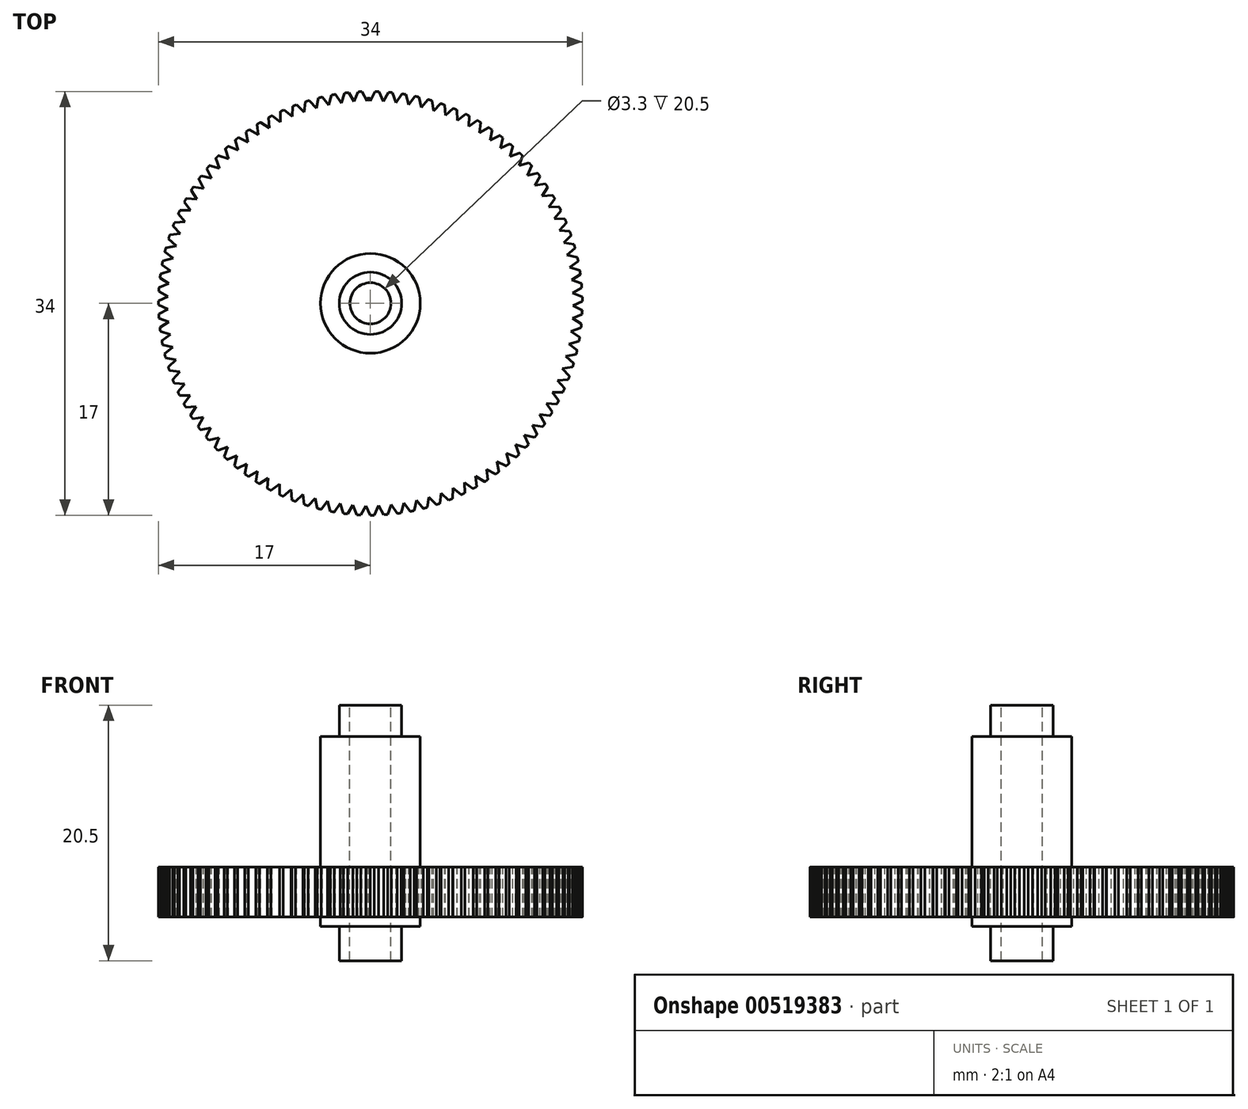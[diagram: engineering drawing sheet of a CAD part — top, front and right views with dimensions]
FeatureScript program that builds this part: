
annotation { "Feature Type Name" : "Feature", "Feature Type Description" : "" }
export const myFeature = defineFeature(function(context is Context, id is Id, definition is map)
    precondition{}
    {
        {
            var Q0;
            Q0=qCreatedBy(makeId("Top.planeOp"),FACE);
            var sketch = newSketch(context, id + "F0", { "sketchPlane" : qUnion([Q0])});
            skCircle(sketch, "E0", {"center": v(0, 0) * mm, "radius": 17 * mm});
            skSolve(sketch);
        }
        {
            var Q0;
            Q0 = qSketchRegion(id + "F0", true);
            extrude(context, id + "F1", {"entities" : qUnion([Q0]), "depth" : 4 * mm, "offsetDistance" : 25 * mm});
        }
        {
            var Q0;
            Q0=makeQuery(id+"F1.opExtrude","CAP_FACE",FACE,{"disambiguationData":[OSD([sQuery(id+"F0.wireOp",EDGE,"E0")])],"isStart":false});
            var sketch = newSketch(context, id + "F2", { "sketchPlane" : qUnion([Q0])});
            skLineSegment(sketch, "E1", {"start": v(-0.37, 17) * mm, "end": v(0, 16.25) * mm});
            skLineSegment(sketch, "E2", {"start": v(0, 16.25) * mm, "end": v(0.38, 17) * mm});
            skLineSegment(sketch, "E3", {"start": v(-0.37, 17) * mm, "end": v(0, 17.76) * mm});
            skLineSegment(sketch, "E4", {"start": v(0, 17.76) * mm, "end": v(0.38, 17) * mm});
            skLineSegment(sketch, "E5.1.0", {"start": v(1.03, 16.21) * mm, "end": v(1.45, 16.94) * mm});
            skLineSegment(sketch, "E5.1.1", {"start": v(0.7, 16.99) * mm, "end": v(1.03, 16.21) * mm});
            skLineSegment(sketch, "E5.1.2", {"start": v(1.12, 17.73) * mm, "end": v(1.45, 16.94) * mm});
            skLineSegment(sketch, "E5.1.3", {"start": v(0.7, 16.99) * mm, "end": v(1.12, 17.73) * mm});
            skLineSegment(sketch, "E5.2.0", {"start": v(2.05, 16.12) * mm, "end": v(2.52, 16.81) * mm});
            skLineSegment(sketch, "E5.2.1", {"start": v(1.77, 16.9) * mm, "end": v(2.05, 16.12) * mm});
            skLineSegment(sketch, "E5.2.2", {"start": v(2.24, 17.62) * mm, "end": v(2.52, 16.81) * mm});
            skLineSegment(sketch, "E5.2.3", {"start": v(1.77, 16.9) * mm, "end": v(2.24, 17.62) * mm});
            skPoint(sketch, "E5.center", {"position": v(0, 0) * mm});
            skLineSegment(sketch, "E5.anchor1", {"start": v(0, 0) * mm, "end": v(0, 16.25) * mm, "construction": true});
            skLineSegment(sketch, "E5.anchor2", {"start": v(0, 0) * mm, "end": v(-0.28, 16.24) * mm, "construction": true});
            skLineSegment(sketch, "E6.1.3.0", {"start": v(3.07, 15.95) * mm, "end": v(3.58, 16.62) * mm});
            skLineSegment(sketch, "E6.3.3.0", {"start": v(2.84, 16.76) * mm, "end": v(3.07, 15.95) * mm});
            skLineSegment(sketch, "E6.6.3.0", {"start": v(3.35, 17.44) * mm, "end": v(3.58, 16.62) * mm});
            skLineSegment(sketch, "E6.9.3.0", {"start": v(2.84, 16.76) * mm, "end": v(3.35, 17.44) * mm});
            skLineSegment(sketch, "E6.1.4.0", {"start": v(4.07, 15.73) * mm, "end": v(4.62, 16.36) * mm});
            skLineSegment(sketch, "E6.3.4.0", {"start": v(3.9, 16.55) * mm, "end": v(4.07, 15.73) * mm});
            skLineSegment(sketch, "E6.6.4.0", {"start": v(4.45, 17.2) * mm, "end": v(4.62, 16.36) * mm});
            skLineSegment(sketch, "E6.9.4.0", {"start": v(3.9, 16.55) * mm, "end": v(4.45, 17.2) * mm});
            skLineSegment(sketch, "E6.1.5.0", {"start": v(5.06, 15.44) * mm, "end": v(5.65, 16.04) * mm});
            skLineSegment(sketch, "E6.3.5.0", {"start": v(4.93, 16.27) * mm, "end": v(5.06, 15.44) * mm});
            skLineSegment(sketch, "E6.6.5.0", {"start": v(5.53, 16.88) * mm, "end": v(5.65, 16.04) * mm});
            skLineSegment(sketch, "E6.9.5.0", {"start": v(4.93, 16.27) * mm, "end": v(5.53, 16.88) * mm});
            skLineSegment(sketch, "E6.1.6.0", {"start": v(6.02, 15.09) * mm, "end": v(6.65, 15.65) * mm});
            skLineSegment(sketch, "E6.3.6.0", {"start": v(5.95, 15.92) * mm, "end": v(6.02, 15.09) * mm});
            skLineSegment(sketch, "E6.6.6.0", {"start": v(6.58, 16.5) * mm, "end": v(6.65, 15.65) * mm});
            skLineSegment(sketch, "E6.9.6.0", {"start": v(5.95, 15.92) * mm, "end": v(6.58, 16.5) * mm});
            skLineSegment(sketch, "E6.1.7.0", {"start": v(6.96, 14.68) * mm, "end": v(7.62, 15.2) * mm});
            skLineSegment(sketch, "E6.3.7.0", {"start": v(6.95, 15.52) * mm, "end": v(6.96, 14.68) * mm});
            skLineSegment(sketch, "E6.6.7.0", {"start": v(7.61, 16.05) * mm, "end": v(7.62, 15.2) * mm});
            skLineSegment(sketch, "E6.9.7.0", {"start": v(6.95, 15.52) * mm, "end": v(7.61, 16.05) * mm});
            skLineSegment(sketch, "E6.1.8.0", {"start": v(7.88, 14.2) * mm, "end": v(8.57, 14.68) * mm});
            skLineSegment(sketch, "E6.3.8.0", {"start": v(7.91, 15.05) * mm, "end": v(7.88, 14.2) * mm});
            skLineSegment(sketch, "E6.6.8.0", {"start": v(8.61, 15.53) * mm, "end": v(8.57, 14.68) * mm});
            skLineSegment(sketch, "E6.9.8.0", {"start": v(7.91, 15.05) * mm, "end": v(8.61, 15.53) * mm});
            skLineSegment(sketch, "E6.1.9.0", {"start": v(8.76, 13.68) * mm, "end": v(9.48, 14.11) * mm});
            skLineSegment(sketch, "E6.3.9.0", {"start": v(8.85, 14.51) * mm, "end": v(8.76, 13.68) * mm});
            skLineSegment(sketch, "E6.6.9.0", {"start": v(9.58, 14.96) * mm, "end": v(9.48, 14.11) * mm});
            skLineSegment(sketch, "E6.9.9.0", {"start": v(8.85, 14.51) * mm, "end": v(9.58, 14.96) * mm});
            skLineSegment(sketch, "E6.1.10.0", {"start": v(9.6, 13.1) * mm, "end": v(10.36, 13.48) * mm});
            skLineSegment(sketch, "E6.3.10.0", {"start": v(9.75, 13.93) * mm, "end": v(9.6, 13.1) * mm});
            skLineSegment(sketch, "E6.6.10.0", {"start": v(10.5, 14.32) * mm, "end": v(10.36, 13.48) * mm});
            skLineSegment(sketch, "E6.9.10.0", {"start": v(9.75, 13.93) * mm, "end": v(10.5, 14.32) * mm});
            skLineSegment(sketch, "E6.1.11.0", {"start": v(10.42, 12.47) * mm, "end": v(11.19, 12.8) * mm});
            skLineSegment(sketch, "E6.3.11.0", {"start": v(10.61, 13.28) * mm, "end": v(10.42, 12.47) * mm});
            skLineSegment(sketch, "E6.6.11.0", {"start": v(11.4, 13.63) * mm, "end": v(11.19, 12.8) * mm});
            skLineSegment(sketch, "E6.9.11.0", {"start": v(10.61, 13.28) * mm, "end": v(11.4, 13.63) * mm});
            skLineSegment(sketch, "E6.1.12.0", {"start": v(11.19, 11.78) * mm, "end": v(11.97, 12.07) * mm});
            skLineSegment(sketch, "E6.3.12.0", {"start": v(11.43, 12.58) * mm, "end": v(11.19, 11.78) * mm});
            skLineSegment(sketch, "E6.6.12.0", {"start": v(12.23, 12.88) * mm, "end": v(11.97, 12.07) * mm});
            skLineSegment(sketch, "E6.9.12.0", {"start": v(11.43, 12.58) * mm, "end": v(12.23, 12.88) * mm});
            skLineSegment(sketch, "E6.1.13.0", {"start": v(11.9, 11.05) * mm, "end": v(12.71, 11.29) * mm});
            skLineSegment(sketch, "E6.3.13.0", {"start": v(12.2, 11.84) * mm, "end": v(11.9, 11.05) * mm});
            skLineSegment(sketch, "E6.6.13.0", {"start": v(13.02, 12.08) * mm, "end": v(12.71, 11.29) * mm});
            skLineSegment(sketch, "E6.9.13.0", {"start": v(12.2, 11.84) * mm, "end": v(13.02, 12.08) * mm});
            skLineSegment(sketch, "E6.1.14.0", {"start": v(12.58, 10.27) * mm, "end": v(13.4, 10.46) * mm});
            skLineSegment(sketch, "E6.3.14.0", {"start": v(12.93, 11.04) * mm, "end": v(12.58, 10.27) * mm});
            skLineSegment(sketch, "E6.6.14.0", {"start": v(13.76, 11.23) * mm, "end": v(13.4, 10.46) * mm});
            skLineSegment(sketch, "E6.9.14.0", {"start": v(12.93, 11.04) * mm, "end": v(13.76, 11.23) * mm});
            skLineSegment(sketch, "E6.1.15.0", {"start": v(13.2, 9.46) * mm, "end": v(14.04, 9.6) * mm});
            skLineSegment(sketch, "E6.3.15.0", {"start": v(13.6, 10.2) * mm, "end": v(13.2, 9.46) * mm});
            skLineSegment(sketch, "E6.6.15.0", {"start": v(14.44, 10.34) * mm, "end": v(14.04, 9.6) * mm});
            skLineSegment(sketch, "E6.9.15.0", {"start": v(13.6, 10.2) * mm, "end": v(14.44, 10.34) * mm});
            skLineSegment(sketch, "E6.1.16.0", {"start": v(13.78, 8.6) * mm, "end": v(14.62, 8.68) * mm});
            skLineSegment(sketch, "E6.3.16.0", {"start": v(14.22, 9.32) * mm, "end": v(13.78, 8.6) * mm});
            skLineSegment(sketch, "E6.6.16.0", {"start": v(15.07, 9.4) * mm, "end": v(14.62, 8.68) * mm});
            skLineSegment(sketch, "E6.9.16.0", {"start": v(14.22, 9.32) * mm, "end": v(15.07, 9.4) * mm});
            skLineSegment(sketch, "E6.1.17.0", {"start": v(14.3, 7.72) * mm, "end": v(15.14, 7.74) * mm});
            skLineSegment(sketch, "E6.3.17.0", {"start": v(14.78, 8.4) * mm, "end": v(14.3, 7.72) * mm});
            skLineSegment(sketch, "E6.6.17.0", {"start": v(15.63, 8.44) * mm, "end": v(15.14, 7.74) * mm});
            skLineSegment(sketch, "E6.9.17.0", {"start": v(14.78, 8.4) * mm, "end": v(15.63, 8.44) * mm});
            skLineSegment(sketch, "E6.1.18.0", {"start": v(14.76, 6.8) * mm, "end": v(15.6, 6.77) * mm});
            skLineSegment(sketch, "E6.3.18.0", {"start": v(15.28, 7.45) * mm, "end": v(14.76, 6.8) * mm});
            skLineSegment(sketch, "E6.6.18.0", {"start": v(16.13, 7.43) * mm, "end": v(15.6, 6.77) * mm});
            skLineSegment(sketch, "E6.9.18.0", {"start": v(15.28, 7.45) * mm, "end": v(16.13, 7.43) * mm});
            skLineSegment(sketch, "E6.1.19.0", {"start": v(15.16, 5.85) * mm, "end": v(16, 5.77) * mm});
            skLineSegment(sketch, "E6.3.19.0", {"start": v(15.72, 6.47) * mm, "end": v(15.16, 5.85) * mm});
            skLineSegment(sketch, "E6.6.19.0", {"start": v(16.57, 6.4) * mm, "end": v(16, 5.77) * mm});
            skLineSegment(sketch, "E6.9.19.0", {"start": v(15.72, 6.47) * mm, "end": v(16.57, 6.4) * mm});
            skLineSegment(sketch, "E6.1.20.0", {"start": v(15.5, 4.88) * mm, "end": v(16.32, 4.75) * mm});
            skLineSegment(sketch, "E6.3.20.0", {"start": v(16.1, 5.46) * mm, "end": v(15.5, 4.88) * mm});
            skLineSegment(sketch, "E6.6.20.0", {"start": v(16.94, 5.33) * mm, "end": v(16.32, 4.75) * mm});
            skLineSegment(sketch, "E6.9.20.0", {"start": v(16.1, 5.46) * mm, "end": v(16.94, 5.33) * mm});
            skLineSegment(sketch, "E6.1.21.0", {"start": v(15.77, 3.89) * mm, "end": v(16.6, 3.7) * mm});
            skLineSegment(sketch, "E6.3.21.0", {"start": v(16.41, 4.43) * mm, "end": v(15.77, 3.89) * mm});
            skLineSegment(sketch, "E6.6.21.0", {"start": v(17.25, 4.25) * mm, "end": v(16.6, 3.7) * mm});
            skLineSegment(sketch, "E6.9.21.0", {"start": v(16.41, 4.43) * mm, "end": v(17.25, 4.25) * mm});
            skLineSegment(sketch, "E6.1.22.0", {"start": v(15.99, 2.88) * mm, "end": v(16.8, 2.65) * mm});
            skLineSegment(sketch, "E6.3.22.0", {"start": v(16.66, 3.39) * mm, "end": v(15.99, 2.88) * mm});
            skLineSegment(sketch, "E6.6.22.0", {"start": v(17.48, 3.15) * mm, "end": v(16.8, 2.65) * mm});
            skLineSegment(sketch, "E6.9.22.0", {"start": v(16.66, 3.39) * mm, "end": v(17.48, 3.15) * mm});
            skLineSegment(sketch, "E6.1.23.0", {"start": v(16.14, 1.87) * mm, "end": v(16.93, 1.58) * mm});
            skLineSegment(sketch, "E6.3.23.0", {"start": v(16.84, 2.32) * mm, "end": v(16.14, 1.87) * mm});
            skLineSegment(sketch, "E6.6.23.0", {"start": v(17.64, 2.04) * mm, "end": v(16.93, 1.58) * mm});
            skLineSegment(sketch, "E6.9.23.0", {"start": v(16.84, 2.32) * mm, "end": v(17.64, 2.04) * mm});
            skLineSegment(sketch, "E6.1.24.0", {"start": v(16.22, 0.84) * mm, "end": v(17, 0.5) * mm});
            skLineSegment(sketch, "E6.3.24.0", {"start": v(16.95, 1.26) * mm, "end": v(16.22, 0.84) * mm});
            skLineSegment(sketch, "E6.6.24.0", {"start": v(17.74, 0.92) * mm, "end": v(17, 0.5) * mm});
            skLineSegment(sketch, "E6.9.24.0", {"start": v(16.95, 1.26) * mm, "end": v(17.74, 0.92) * mm});
            skLineSegment(sketch, "E6.1.25.0", {"start": v(16.24, -0.19) * mm, "end": v(17, -0.57) * mm});
            skLineSegment(sketch, "E6.3.25.0", {"start": v(17, 0.18) * mm, "end": v(16.24, -0.19) * mm});
            skLineSegment(sketch, "E6.6.25.0", {"start": v(17.76, -0.2) * mm, "end": v(17, -0.57) * mm});
            skLineSegment(sketch, "E6.9.25.0", {"start": v(17, 0.18) * mm, "end": v(17.76, -0.2) * mm});
            skLineSegment(sketch, "E6.1.26.0", {"start": v(16.2, -1.21) * mm, "end": v(16.92, -1.64) * mm});
            skLineSegment(sketch, "E6.3.26.0", {"start": v(16.98, -0.9) * mm, "end": v(16.2, -1.21) * mm});
            skLineSegment(sketch, "E6.6.26.0", {"start": v(17.71, -1.33) * mm, "end": v(16.92, -1.64) * mm});
            skLineSegment(sketch, "E6.9.26.0", {"start": v(16.98, -0.9) * mm, "end": v(17.71, -1.33) * mm});
            skLineSegment(sketch, "E6.1.27.0", {"start": v(16.1, -2.24) * mm, "end": v(16.78, -2.71) * mm});
            skLineSegment(sketch, "E6.3.27.0", {"start": v(16.89, -1.97) * mm, "end": v(16.1, -2.24) * mm});
            skLineSegment(sketch, "E6.6.27.0", {"start": v(17.6, -2.44) * mm, "end": v(16.78, -2.71) * mm});
            skLineSegment(sketch, "E6.9.27.0", {"start": v(16.89, -1.97) * mm, "end": v(17.6, -2.44) * mm});
            skLineSegment(sketch, "E6.1.28.0", {"start": v(15.92, -3.25) * mm, "end": v(16.58, -3.77) * mm});
            skLineSegment(sketch, "E6.3.28.0", {"start": v(16.73, -3.03) * mm, "end": v(15.92, -3.25) * mm});
            skLineSegment(sketch, "E6.6.28.0", {"start": v(17.4, -3.55) * mm, "end": v(16.58, -3.77) * mm});
            skLineSegment(sketch, "E6.9.28.0", {"start": v(16.73, -3.03) * mm, "end": v(17.4, -3.55) * mm});
            skLineSegment(sketch, "E6.1.29.0", {"start": v(15.68, -4.25) * mm, "end": v(16.3, -4.8) * mm});
            skLineSegment(sketch, "E6.3.29.0", {"start": v(16.5, -4.08) * mm, "end": v(15.68, -4.25) * mm});
            skLineSegment(sketch, "E6.6.29.0", {"start": v(17.14, -4.65) * mm, "end": v(16.3, -4.8) * mm});
            skLineSegment(sketch, "E6.9.29.0", {"start": v(16.5, -4.08) * mm, "end": v(17.14, -4.65) * mm});
            skLineSegment(sketch, "E6.1.30.0", {"start": v(15.38, -5.23) * mm, "end": v(15.97, -5.83) * mm});
            skLineSegment(sketch, "E6.3.30.0", {"start": v(16.21, -5.12) * mm, "end": v(15.38, -5.23) * mm});
            skLineSegment(sketch, "E6.6.30.0", {"start": v(16.82, -5.72) * mm, "end": v(15.97, -5.83) * mm});
            skLineSegment(sketch, "E6.9.30.0", {"start": v(16.21, -5.12) * mm, "end": v(16.82, -5.72) * mm});
            skLineSegment(sketch, "E6.1.31.0", {"start": v(15.02, -6.2) * mm, "end": v(15.57, -6.83) * mm});
            skLineSegment(sketch, "E6.3.31.0", {"start": v(15.85, -6.13) * mm, "end": v(15.02, -6.2) * mm});
            skLineSegment(sketch, "E6.6.31.0", {"start": v(16.42, -6.77) * mm, "end": v(15.57, -6.83) * mm});
            skLineSegment(sketch, "E6.9.31.0", {"start": v(15.85, -6.13) * mm, "end": v(16.42, -6.77) * mm});
            skLineSegment(sketch, "E6.1.32.0", {"start": v(14.6, -7.13) * mm, "end": v(15.1, -7.8) * mm});
            skLineSegment(sketch, "E6.3.32.0", {"start": v(15.44, -7.12) * mm, "end": v(14.6, -7.13) * mm});
            skLineSegment(sketch, "E6.6.32.0", {"start": v(15.96, -7.8) * mm, "end": v(15.1, -7.8) * mm});
            skLineSegment(sketch, "E6.9.32.0", {"start": v(15.44, -7.12) * mm, "end": v(15.96, -7.8) * mm});
            skLineSegment(sketch, "E6.1.33.0", {"start": v(14.12, -8.04) * mm, "end": v(14.58, -8.74) * mm});
            skLineSegment(sketch, "E6.3.33.0", {"start": v(14.95, -8.09) * mm, "end": v(14.12, -8.04) * mm});
            skLineSegment(sketch, "E6.6.33.0", {"start": v(15.43, -8.8) * mm, "end": v(14.58, -8.74) * mm});
            skLineSegment(sketch, "E6.9.33.0", {"start": v(14.95, -8.09) * mm, "end": v(15.43, -8.8) * mm});
            skLineSegment(sketch, "E6.1.34.0", {"start": v(13.58, -8.92) * mm, "end": v(14, -9.64) * mm});
            skLineSegment(sketch, "E6.3.34.0", {"start": v(14.41, -9.02) * mm, "end": v(13.58, -8.92) * mm});
            skLineSegment(sketch, "E6.6.34.0", {"start": v(14.85, -9.75) * mm, "end": v(14, -9.64) * mm});
            skLineSegment(sketch, "E6.9.34.0", {"start": v(14.41, -9.02) * mm, "end": v(14.85, -9.75) * mm});
            skLineSegment(sketch, "E6.1.35.0", {"start": v(12.99, -9.76) * mm, "end": v(13.36, -10.5) * mm});
            skLineSegment(sketch, "E6.3.35.0", {"start": v(13.81, -9.9) * mm, "end": v(12.99, -9.76) * mm});
            skLineSegment(sketch, "E6.6.35.0", {"start": v(14.2, -10.67) * mm, "end": v(13.36, -10.5) * mm});
            skLineSegment(sketch, "E6.9.35.0", {"start": v(13.81, -9.9) * mm, "end": v(14.2, -10.67) * mm});
            skLineSegment(sketch, "E6.1.36.0", {"start": v(12.35, -10.56) * mm, "end": v(12.67, -11.33) * mm});
            skLineSegment(sketch, "E6.3.36.0", {"start": v(13.16, -10.76) * mm, "end": v(12.35, -10.56) * mm});
            skLineSegment(sketch, "E6.6.36.0", {"start": v(13.5, -11.55) * mm, "end": v(12.67, -11.33) * mm});
            skLineSegment(sketch, "E6.9.36.0", {"start": v(13.16, -10.76) * mm, "end": v(13.5, -11.55) * mm});
            skLineSegment(sketch, "E6.1.37.0", {"start": v(11.65, -11.32) * mm, "end": v(11.93, -12.11) * mm});
            skLineSegment(sketch, "E6.3.37.0", {"start": v(12.45, -11.57) * mm, "end": v(11.65, -11.32) * mm});
            skLineSegment(sketch, "E6.6.37.0", {"start": v(12.74, -12.38) * mm, "end": v(11.93, -12.11) * mm});
            skLineSegment(sketch, "E6.9.37.0", {"start": v(12.45, -11.57) * mm, "end": v(12.74, -12.38) * mm});
            skLineSegment(sketch, "E6.1.38.0", {"start": v(10.91, -12.03) * mm, "end": v(11.14, -12.84) * mm});
            skLineSegment(sketch, "E6.3.38.0", {"start": v(11.7, -12.34) * mm, "end": v(10.91, -12.03) * mm});
            skLineSegment(sketch, "E6.6.38.0", {"start": v(11.93, -13.16) * mm, "end": v(11.14, -12.84) * mm});
            skLineSegment(sketch, "E6.9.38.0", {"start": v(11.7, -12.34) * mm, "end": v(11.93, -13.16) * mm});
            skLineSegment(sketch, "E6.1.39.0", {"start": v(10.13, -12.7) * mm, "end": v(10.3, -13.52) * mm});
            skLineSegment(sketch, "E6.3.39.0", {"start": v(10.9, -13.05) * mm, "end": v(10.13, -12.7) * mm});
            skLineSegment(sketch, "E6.6.39.0", {"start": v(11.08, -13.89) * mm, "end": v(10.3, -13.52) * mm});
            skLineSegment(sketch, "E6.9.39.0", {"start": v(10.9, -13.05) * mm, "end": v(11.08, -13.89) * mm});
            skLineSegment(sketch, "E6.1.40.0", {"start": v(9.3, -13.32) * mm, "end": v(9.43, -14.15) * mm});
            skLineSegment(sketch, "E6.3.40.0", {"start": v(10.04, -13.72) * mm, "end": v(9.3, -13.32) * mm});
            skLineSegment(sketch, "E6.6.40.0", {"start": v(10.18, -14.56) * mm, "end": v(9.43, -14.15) * mm});
            skLineSegment(sketch, "E6.9.40.0", {"start": v(10.04, -13.72) * mm, "end": v(10.18, -14.56) * mm});
            skLineSegment(sketch, "E6.1.41.0", {"start": v(8.45, -13.88) * mm, "end": v(8.52, -14.71) * mm});
            skLineSegment(sketch, "E6.3.41.0", {"start": v(9.16, -14.32) * mm, "end": v(8.45, -13.88) * mm});
            skLineSegment(sketch, "E6.6.41.0", {"start": v(9.23, -15.17) * mm, "end": v(8.52, -14.71) * mm});
            skLineSegment(sketch, "E6.9.41.0", {"start": v(9.16, -14.32) * mm, "end": v(9.23, -15.17) * mm});
            skLineSegment(sketch, "E6.1.42.0", {"start": v(7.55, -14.38) * mm, "end": v(7.57, -15.22) * mm});
            skLineSegment(sketch, "E6.3.42.0", {"start": v(8.23, -14.87) * mm, "end": v(7.55, -14.38) * mm});
            skLineSegment(sketch, "E6.6.42.0", {"start": v(8.26, -15.73) * mm, "end": v(7.57, -15.22) * mm});
            skLineSegment(sketch, "E6.9.42.0", {"start": v(8.23, -14.87) * mm, "end": v(8.26, -15.73) * mm});
            skLineSegment(sketch, "E6.1.43.0", {"start": v(6.63, -14.83) * mm, "end": v(6.59, -15.67) * mm});
            skLineSegment(sketch, "E6.3.43.0", {"start": v(7.27, -15.37) * mm, "end": v(6.63, -14.83) * mm});
            skLineSegment(sketch, "E6.6.43.0", {"start": v(7.24, -16.22) * mm, "end": v(6.59, -15.67) * mm});
            skLineSegment(sketch, "E6.9.43.0", {"start": v(7.27, -15.37) * mm, "end": v(7.24, -16.22) * mm});
            skLineSegment(sketch, "E6.1.44.0", {"start": v(5.67, -15.22) * mm, "end": v(5.59, -16.06) * mm});
            skLineSegment(sketch, "E6.3.44.0", {"start": v(6.29, -15.8) * mm, "end": v(5.67, -15.22) * mm});
            skLineSegment(sketch, "E6.6.44.0", {"start": v(6.2, -16.64) * mm, "end": v(5.59, -16.06) * mm});
            skLineSegment(sketch, "E6.9.44.0", {"start": v(6.29, -15.8) * mm, "end": v(6.2, -16.64) * mm});
            skLineSegment(sketch, "E6.1.45.0", {"start": v(4.7, -15.55) * mm, "end": v(4.56, -16.38) * mm});
            skLineSegment(sketch, "E6.3.45.0", {"start": v(5.28, -16.16) * mm, "end": v(4.7, -15.55) * mm});
            skLineSegment(sketch, "E6.6.45.0", {"start": v(5.14, -17) * mm, "end": v(4.56, -16.38) * mm});
            skLineSegment(sketch, "E6.9.45.0", {"start": v(5.28, -16.16) * mm, "end": v(5.14, -17) * mm});
            skLineSegment(sketch, "E6.1.46.0", {"start": v(3.7, -15.82) * mm, "end": v(3.51, -16.63) * mm});
            skLineSegment(sketch, "E6.3.46.0", {"start": v(4.24, -16.46) * mm, "end": v(3.7, -15.82) * mm});
            skLineSegment(sketch, "E6.6.46.0", {"start": v(4.05, -17.3) * mm, "end": v(3.51, -16.63) * mm});
            skLineSegment(sketch, "E6.9.46.0", {"start": v(4.24, -16.46) * mm, "end": v(4.05, -17.3) * mm});
            skLineSegment(sketch, "E6.1.47.0", {"start": v(2.7, -16.02) * mm, "end": v(2.45, -16.82) * mm});
            skLineSegment(sketch, "E6.3.47.0", {"start": v(3.2, -16.7) * mm, "end": v(2.7, -16.02) * mm});
            skLineSegment(sketch, "E6.6.47.0", {"start": v(2.95, -17.52) * mm, "end": v(2.45, -16.82) * mm});
            skLineSegment(sketch, "E6.9.47.0", {"start": v(3.2, -16.7) * mm, "end": v(2.95, -17.52) * mm});
            skLineSegment(sketch, "E6.1.48.0", {"start": v(1.68, -16.16) * mm, "end": v(1.39, -16.94) * mm});
            skLineSegment(sketch, "E6.3.48.0", {"start": v(2.13, -16.87) * mm, "end": v(1.68, -16.16) * mm});
            skLineSegment(sketch, "E6.6.48.0", {"start": v(1.84, -17.67) * mm, "end": v(1.39, -16.94) * mm});
            skLineSegment(sketch, "E6.9.48.0", {"start": v(2.13, -16.87) * mm, "end": v(1.84, -17.67) * mm});
            skLineSegment(sketch, "E6.1.49.0", {"start": v(0.66, -16.23) * mm, "end": v(0.31, -17) * mm});
            skLineSegment(sketch, "E6.3.49.0", {"start": v(1.06, -16.97) * mm, "end": v(0.66, -16.23) * mm});
            skLineSegment(sketch, "E6.6.49.0", {"start": v(0.72, -17.75) * mm, "end": v(0.31, -17) * mm});
            skLineSegment(sketch, "E6.9.49.0", {"start": v(1.06, -16.97) * mm, "end": v(0.72, -17.75) * mm});
            skLineSegment(sketch, "E6.1.50.0", {"start": v(-0.37, -16.24) * mm, "end": v(-0.76, -16.98) * mm});
            skLineSegment(sketch, "E6.3.50.0", {"start": v(-0.01, -17) * mm, "end": v(-0.37, -16.24) * mm});
            skLineSegment(sketch, "E6.6.50.0", {"start": v(-0.4, -17.76) * mm, "end": v(-0.76, -16.98) * mm});
            skLineSegment(sketch, "E6.9.50.0", {"start": v(-0.01, -17) * mm, "end": v(-0.4, -17.76) * mm});
            skLineSegment(sketch, "E6.1.51.0", {"start": v(-1.4, -16.19) * mm, "end": v(-1.84, -16.9) * mm});
            skLineSegment(sketch, "E6.3.51.0", {"start": v(-1.09, -16.97) * mm, "end": v(-1.4, -16.19) * mm});
            skLineSegment(sketch, "E6.6.51.0", {"start": v(-1.53, -17.7) * mm, "end": v(-1.84, -16.9) * mm});
            skLineSegment(sketch, "E6.9.51.0", {"start": v(-1.09, -16.97) * mm, "end": v(-1.53, -17.7) * mm});
            skLineSegment(sketch, "E6.1.52.0", {"start": v(-2.42, -16.06) * mm, "end": v(-2.9, -16.75) * mm});
            skLineSegment(sketch, "E6.3.52.0", {"start": v(-2.16, -16.86) * mm, "end": v(-2.42, -16.06) * mm});
            skLineSegment(sketch, "E6.6.52.0", {"start": v(-2.65, -17.56) * mm, "end": v(-2.9, -16.75) * mm});
            skLineSegment(sketch, "E6.9.52.0", {"start": v(-2.16, -16.86) * mm, "end": v(-2.65, -17.56) * mm});
            skLineSegment(sketch, "E6.1.53.0", {"start": v(-3.43, -15.88) * mm, "end": v(-3.96, -16.53) * mm});
            skLineSegment(sketch, "E6.3.53.0", {"start": v(-3.22, -16.7) * mm, "end": v(-3.43, -15.88) * mm});
            skLineSegment(sketch, "E6.6.53.0", {"start": v(-3.75, -17.36) * mm, "end": v(-3.96, -16.53) * mm});
            skLineSegment(sketch, "E6.9.53.0", {"start": v(-3.22, -16.7) * mm, "end": v(-3.75, -17.36) * mm});
            skLineSegment(sketch, "E6.1.54.0", {"start": v(-4.43, -15.63) * mm, "end": v(-5, -16.25) * mm});
            skLineSegment(sketch, "E6.3.54.0", {"start": v(-4.27, -16.45) * mm, "end": v(-4.43, -15.63) * mm});
            skLineSegment(sketch, "E6.6.54.0", {"start": v(-4.84, -17.09) * mm, "end": v(-5, -16.25) * mm});
            skLineSegment(sketch, "E6.9.54.0", {"start": v(-4.27, -16.45) * mm, "end": v(-4.84, -17.09) * mm});
            skLineSegment(sketch, "E6.1.55.0", {"start": v(-5.4, -15.32) * mm, "end": v(-6.01, -15.9) * mm});
            skLineSegment(sketch, "E6.3.55.0", {"start": v(-5.3, -16.15) * mm, "end": v(-5.4, -15.32) * mm});
            skLineSegment(sketch, "E6.6.55.0", {"start": v(-5.91, -16.75) * mm, "end": v(-6.01, -15.9) * mm});
            skLineSegment(sketch, "E6.9.55.0", {"start": v(-5.3, -16.15) * mm, "end": v(-5.91, -16.75) * mm});
            skLineSegment(sketch, "E6.1.56.0", {"start": v(-6.37, -14.95) * mm, "end": v(-7, -15.49) * mm});
            skLineSegment(sketch, "E6.3.56.0", {"start": v(-6.32, -15.78) * mm, "end": v(-6.37, -14.95) * mm});
            skLineSegment(sketch, "E6.6.56.0", {"start": v(-6.96, -16.34) * mm, "end": v(-7, -15.49) * mm});
            skLineSegment(sketch, "E6.9.56.0", {"start": v(-6.32, -15.78) * mm, "end": v(-6.96, -16.34) * mm});
            skLineSegment(sketch, "E6.1.57.0", {"start": v(-7.3, -14.51) * mm, "end": v(-7.97, -15.02) * mm});
            skLineSegment(sketch, "E6.3.57.0", {"start": v(-7.3, -15.35) * mm, "end": v(-7.3, -14.51) * mm});
            skLineSegment(sketch, "E6.6.57.0", {"start": v(-7.98, -15.87) * mm, "end": v(-7.97, -15.02) * mm});
            skLineSegment(sketch, "E6.9.57.0", {"start": v(-7.3, -15.35) * mm, "end": v(-7.98, -15.87) * mm});
            skLineSegment(sketch, "E6.1.58.0", {"start": v(-8.2, -14.02) * mm, "end": v(-8.9, -14.48) * mm});
            skLineSegment(sketch, "E6.3.58.0", {"start": v(-8.26, -14.86) * mm, "end": v(-8.2, -14.02) * mm});
            skLineSegment(sketch, "E6.6.58.0", {"start": v(-8.97, -15.33) * mm, "end": v(-8.9, -14.48) * mm});
            skLineSegment(sketch, "E6.9.58.0", {"start": v(-8.26, -14.86) * mm, "end": v(-8.97, -15.33) * mm});
            skLineSegment(sketch, "E6.1.59.0", {"start": v(-9.07, -13.48) * mm, "end": v(-9.8, -13.89) * mm});
            skLineSegment(sketch, "E6.3.59.0", {"start": v(-9.18, -14.3) * mm, "end": v(-9.07, -13.48) * mm});
            skLineSegment(sketch, "E6.6.59.0", {"start": v(-9.92, -14.73) * mm, "end": v(-9.8, -13.89) * mm});
            skLineSegment(sketch, "E6.9.59.0", {"start": v(-9.18, -14.3) * mm, "end": v(-9.92, -14.73) * mm});
            skLineSegment(sketch, "E6.1.60.0", {"start": v(-9.9, -12.88) * mm, "end": v(-10.66, -13.24) * mm});
            skLineSegment(sketch, "E6.3.60.0", {"start": v(-10.07, -13.7) * mm, "end": v(-9.9, -12.88) * mm});
            skLineSegment(sketch, "E6.6.60.0", {"start": v(-10.83, -14.08) * mm, "end": v(-10.66, -13.24) * mm});
            skLineSegment(sketch, "E6.9.60.0", {"start": v(-10.07, -13.7) * mm, "end": v(-10.83, -14.08) * mm});
            skLineSegment(sketch, "E6.1.61.0", {"start": v(-10.7, -12.22) * mm, "end": v(-11.48, -12.54) * mm});
            skLineSegment(sketch, "E6.3.61.0", {"start": v(-10.91, -13.03) * mm, "end": v(-10.7, -12.22) * mm});
            skLineSegment(sketch, "E6.6.61.0", {"start": v(-11.7, -13.36) * mm, "end": v(-11.48, -12.54) * mm});
            skLineSegment(sketch, "E6.9.61.0", {"start": v(-10.91, -13.03) * mm, "end": v(-11.7, -13.36) * mm});
            skLineSegment(sketch, "E6.1.62.0", {"start": v(-11.45, -11.52) * mm, "end": v(-12.25, -11.79) * mm});
            skLineSegment(sketch, "E6.3.62.0", {"start": v(-11.72, -12.32) * mm, "end": v(-11.45, -11.52) * mm});
            skLineSegment(sketch, "E6.6.62.0", {"start": v(-12.52, -12.6) * mm, "end": v(-12.25, -11.79) * mm});
            skLineSegment(sketch, "E6.9.62.0", {"start": v(-11.72, -12.32) * mm, "end": v(-12.52, -12.6) * mm});
            skLineSegment(sketch, "E6.1.63.0", {"start": v(-12.16, -10.77) * mm, "end": v(-12.97, -11) * mm});
            skLineSegment(sketch, "E6.3.63.0", {"start": v(-12.47, -11.55) * mm, "end": v(-12.16, -10.77) * mm});
            skLineSegment(sketch, "E6.6.63.0", {"start": v(-13.3, -11.78) * mm, "end": v(-12.97, -11) * mm});
            skLineSegment(sketch, "E6.9.63.0", {"start": v(-12.47, -11.55) * mm, "end": v(-13.3, -11.78) * mm});
            skLineSegment(sketch, "E6.1.64.0", {"start": v(-12.82, -9.98) * mm, "end": v(-13.64, -10.15) * mm});
            skLineSegment(sketch, "E6.3.64.0", {"start": v(-13.18, -10.74) * mm, "end": v(-12.82, -9.98) * mm});
            skLineSegment(sketch, "E6.6.64.0", {"start": v(-14.01, -10.92) * mm, "end": v(-13.64, -10.15) * mm});
            skLineSegment(sketch, "E6.9.64.0", {"start": v(-13.18, -10.74) * mm, "end": v(-14.01, -10.92) * mm});
            skLineSegment(sketch, "E6.1.65.0", {"start": v(-13.42, -9.15) * mm, "end": v(-14.25, -9.27) * mm});
            skLineSegment(sketch, "E6.3.65.0", {"start": v(-13.83, -9.89) * mm, "end": v(-13.42, -9.15) * mm});
            skLineSegment(sketch, "E6.6.65.0", {"start": v(-14.67, -10) * mm, "end": v(-14.25, -9.27) * mm});
            skLineSegment(sketch, "E6.9.65.0", {"start": v(-13.83, -9.89) * mm, "end": v(-14.67, -10) * mm});
            skLineSegment(sketch, "E6.1.66.0", {"start": v(-13.97, -8.29) * mm, "end": v(-14.81, -8.35) * mm});
            skLineSegment(sketch, "E6.3.66.0", {"start": v(-14.43, -9) * mm, "end": v(-13.97, -8.29) * mm});
            skLineSegment(sketch, "E6.6.66.0", {"start": v(-15.28, -9.06) * mm, "end": v(-14.81, -8.35) * mm});
            skLineSegment(sketch, "E6.9.66.0", {"start": v(-14.43, -9) * mm, "end": v(-15.28, -9.06) * mm});
            skLineSegment(sketch, "E6.1.67.0", {"start": v(-14.47, -7.39) * mm, "end": v(-15.3, -7.4) * mm});
            skLineSegment(sketch, "E6.3.67.0", {"start": v(-14.97, -8.06) * mm, "end": v(-14.47, -7.39) * mm});
            skLineSegment(sketch, "E6.6.67.0", {"start": v(-15.82, -8.08) * mm, "end": v(-15.3, -7.4) * mm});
            skLineSegment(sketch, "E6.9.67.0", {"start": v(-14.97, -8.06) * mm, "end": v(-15.82, -8.08) * mm});
            skLineSegment(sketch, "E6.1.68.0", {"start": v(-14.9, -6.46) * mm, "end": v(-15.75, -6.4) * mm});
            skLineSegment(sketch, "E6.3.68.0", {"start": v(-15.45, -7.1) * mm, "end": v(-14.9, -6.46) * mm});
            skLineSegment(sketch, "E6.6.68.0", {"start": v(-16.3, -7.06) * mm, "end": v(-15.75, -6.4) * mm});
            skLineSegment(sketch, "E6.9.68.0", {"start": v(-15.45, -7.1) * mm, "end": v(-16.3, -7.06) * mm});
            skLineSegment(sketch, "E6.1.69.0", {"start": v(-15.29, -5.5) * mm, "end": v(-16.12, -5.4) * mm});
            skLineSegment(sketch, "E6.3.69.0", {"start": v(-15.87, -6.1) * mm, "end": v(-15.29, -5.5) * mm});
            skLineSegment(sketch, "E6.6.69.0", {"start": v(-16.71, -6.01) * mm, "end": v(-16.12, -5.4) * mm});
            skLineSegment(sketch, "E6.9.69.0", {"start": v(-15.87, -6.1) * mm, "end": v(-16.71, -6.01) * mm});
            skLineSegment(sketch, "E6.1.70.0", {"start": v(-15.6, -4.52) * mm, "end": v(-16.43, -4.37) * mm});
            skLineSegment(sketch, "E6.3.70.0", {"start": v(-16.22, -5.1) * mm, "end": v(-15.6, -4.52) * mm});
            skLineSegment(sketch, "E6.6.70.0", {"start": v(-17.06, -4.94) * mm, "end": v(-16.43, -4.37) * mm});
            skLineSegment(sketch, "E6.9.70.0", {"start": v(-16.22, -5.1) * mm, "end": v(-17.06, -4.94) * mm});
            skLineSegment(sketch, "E6.1.71.0", {"start": v(-15.86, -3.53) * mm, "end": v(-16.67, -3.32) * mm});
            skLineSegment(sketch, "E6.3.71.0", {"start": v(-16.5, -4.05) * mm, "end": v(-15.86, -3.53) * mm});
            skLineSegment(sketch, "E6.6.71.0", {"start": v(-17.34, -3.86) * mm, "end": v(-16.67, -3.32) * mm});
            skLineSegment(sketch, "E6.9.71.0", {"start": v(-16.5, -4.05) * mm, "end": v(-17.34, -3.86) * mm});
            skLineSegment(sketch, "E6.1.72.0", {"start": v(-16.05, -2.52) * mm, "end": v(-16.85, -2.26) * mm});
            skLineSegment(sketch, "E6.3.72.0", {"start": v(-16.73, -3) * mm, "end": v(-16.05, -2.52) * mm});
            skLineSegment(sketch, "E6.6.72.0", {"start": v(-17.55, -2.75) * mm, "end": v(-16.85, -2.26) * mm});
            skLineSegment(sketch, "E6.9.72.0", {"start": v(-16.73, -3) * mm, "end": v(-17.55, -2.75) * mm});
            skLineSegment(sketch, "E6.1.73.0", {"start": v(-16.18, -1.5) * mm, "end": v(-16.96, -1.2) * mm});
            skLineSegment(sketch, "E6.3.73.0", {"start": v(-16.89, -1.94) * mm, "end": v(-16.18, -1.5) * mm});
            skLineSegment(sketch, "E6.6.73.0", {"start": v(-17.69, -1.64) * mm, "end": v(-16.96, -1.2) * mm});
            skLineSegment(sketch, "E6.9.73.0", {"start": v(-16.89, -1.94) * mm, "end": v(-17.69, -1.64) * mm});
            skLineSegment(sketch, "E6.1.74.0", {"start": v(-16.24, -0.47) * mm, "end": v(-17, -0.12) * mm});
            skLineSegment(sketch, "E6.3.74.0", {"start": v(-16.98, -0.87) * mm, "end": v(-16.24, -0.47) * mm});
            skLineSegment(sketch, "E6.6.74.0", {"start": v(-17.75, -0.51) * mm, "end": v(-17, -0.12) * mm});
            skLineSegment(sketch, "E6.9.74.0", {"start": v(-16.98, -0.87) * mm, "end": v(-17.75, -0.51) * mm});
            skLineSegment(sketch, "E6.1.75.0", {"start": v(-16.24, 0.56) * mm, "end": v(-16.97, 0.96) * mm});
            skLineSegment(sketch, "E6.3.75.0", {"start": v(-17, 0.2) * mm, "end": v(-16.24, 0.56) * mm});
            skLineSegment(sketch, "E6.6.75.0", {"start": v(-17.75, 0.61) * mm, "end": v(-16.97, 0.96) * mm});
            skLineSegment(sketch, "E6.9.75.0", {"start": v(-17, 0.2) * mm, "end": v(-17.75, 0.61) * mm});
            skLineSegment(sketch, "E6.1.76.0", {"start": v(-16.17, 1.58) * mm, "end": v(-16.88, 2.03) * mm});
            skLineSegment(sketch, "E6.3.76.0", {"start": v(-16.95, 1.28) * mm, "end": v(-16.17, 1.58) * mm});
            skLineSegment(sketch, "E6.6.76.0", {"start": v(-17.68, 1.73) * mm, "end": v(-16.88, 2.03) * mm});
            skLineSegment(sketch, "E6.9.76.0", {"start": v(-16.95, 1.28) * mm, "end": v(-17.68, 1.73) * mm});
            skLineSegment(sketch, "E6.1.77.0", {"start": v(-16.04, 2.6) * mm, "end": v(-16.72, 3.1) * mm});
            skLineSegment(sketch, "E6.3.77.0", {"start": v(-16.84, 2.35) * mm, "end": v(-16.04, 2.6) * mm});
            skLineSegment(sketch, "E6.6.77.0", {"start": v(-17.53, 2.85) * mm, "end": v(-16.72, 3.1) * mm});
            skLineSegment(sketch, "E6.9.77.0", {"start": v(-16.84, 2.35) * mm, "end": v(-17.53, 2.85) * mm});
            skLineSegment(sketch, "E6.1.78.0", {"start": v(-15.84, 3.61) * mm, "end": v(-16.49, 4.15) * mm});
            skLineSegment(sketch, "E6.3.78.0", {"start": v(-16.65, 3.41) * mm, "end": v(-15.84, 3.61) * mm});
            skLineSegment(sketch, "E6.6.78.0", {"start": v(-17.32, 3.95) * mm, "end": v(-16.49, 4.15) * mm});
            skLineSegment(sketch, "E6.9.78.0", {"start": v(-16.65, 3.41) * mm, "end": v(-17.32, 3.95) * mm});
            skLineSegment(sketch, "E6.1.79.0", {"start": v(-15.58, 4.6) * mm, "end": v(-16.2, 5.18) * mm});
            skLineSegment(sketch, "E6.3.79.0", {"start": v(-16.4, 4.46) * mm, "end": v(-15.58, 4.6) * mm});
            skLineSegment(sketch, "E6.6.79.0", {"start": v(-17.03, 5.04) * mm, "end": v(-16.2, 5.18) * mm});
            skLineSegment(sketch, "E6.9.79.0", {"start": v(-16.4, 4.46) * mm, "end": v(-17.03, 5.04) * mm});
            skLineSegment(sketch, "E6.1.80.0", {"start": v(-15.26, 5.58) * mm, "end": v(-15.83, 6.2) * mm});
            skLineSegment(sketch, "E6.3.80.0", {"start": v(-16.09, 5.49) * mm, "end": v(-15.26, 5.58) * mm});
            skLineSegment(sketch, "E6.6.80.0", {"start": v(-16.68, 6.1) * mm, "end": v(-15.83, 6.2) * mm});
            skLineSegment(sketch, "E6.9.80.0", {"start": v(-16.09, 5.49) * mm, "end": v(-16.68, 6.1) * mm});
            skLineSegment(sketch, "E6.1.81.0", {"start": v(-14.87, 6.54) * mm, "end": v(-15.4, 7.18) * mm});
            skLineSegment(sketch, "E6.3.81.0", {"start": v(-15.71, 6.5) * mm, "end": v(-14.87, 6.54) * mm});
            skLineSegment(sketch, "E6.6.81.0", {"start": v(-16.26, 7.15) * mm, "end": v(-15.4, 7.18) * mm});
            skLineSegment(sketch, "E6.9.81.0", {"start": v(-15.71, 6.5) * mm, "end": v(-16.26, 7.15) * mm});
            skLineSegment(sketch, "E6.1.82.0", {"start": v(-14.43, 7.46) * mm, "end": v(-14.92, 8.14) * mm});
            skLineSegment(sketch, "E6.3.82.0", {"start": v(-15.27, 7.48) * mm, "end": v(-14.43, 7.46) * mm});
            skLineSegment(sketch, "E6.6.82.0", {"start": v(-15.78, 8.16) * mm, "end": v(-14.92, 8.14) * mm});
            skLineSegment(sketch, "E6.9.82.0", {"start": v(-15.27, 7.48) * mm, "end": v(-15.78, 8.16) * mm});
            skLineSegment(sketch, "E6.1.83.0", {"start": v(-13.93, 8.36) * mm, "end": v(-14.38, 9.07) * mm});
            skLineSegment(sketch, "E6.3.83.0", {"start": v(-14.76, 8.43) * mm, "end": v(-13.93, 8.36) * mm});
            skLineSegment(sketch, "E6.6.83.0", {"start": v(-15.23, 9.14) * mm, "end": v(-14.38, 9.07) * mm});
            skLineSegment(sketch, "E6.9.83.0", {"start": v(-14.76, 8.43) * mm, "end": v(-15.23, 9.14) * mm});
            skLineSegment(sketch, "E6.1.84.0", {"start": v(-13.37, 9.23) * mm, "end": v(-13.78, 9.96) * mm});
            skLineSegment(sketch, "E6.3.84.0", {"start": v(-14.2, 9.34) * mm, "end": v(-13.37, 9.23) * mm});
            skLineSegment(sketch, "E6.6.84.0", {"start": v(-14.62, 10.09) * mm, "end": v(-13.78, 9.96) * mm});
            skLineSegment(sketch, "E6.9.84.0", {"start": v(-14.2, 9.34) * mm, "end": v(-14.62, 10.09) * mm});
            skLineSegment(sketch, "E6.1.85.0", {"start": v(-12.76, 10.05) * mm, "end": v(-13.12, 10.81) * mm});
            skLineSegment(sketch, "E6.3.85.0", {"start": v(-13.58, 10.22) * mm, "end": v(-12.76, 10.05) * mm});
            skLineSegment(sketch, "E6.6.85.0", {"start": v(-13.95, 11) * mm, "end": v(-13.12, 10.81) * mm});
            skLineSegment(sketch, "E6.9.85.0", {"start": v(-13.58, 10.22) * mm, "end": v(-13.95, 11) * mm});
            skLineSegment(sketch, "E6.1.86.0", {"start": v(-12.1, 10.84) * mm, "end": v(-12.4, 11.62) * mm});
            skLineSegment(sketch, "E6.3.86.0", {"start": v(-12.9, 11.06) * mm, "end": v(-12.1, 10.84) * mm});
            skLineSegment(sketch, "E6.6.86.0", {"start": v(-13.23, 11.85) * mm, "end": v(-12.4, 11.62) * mm});
            skLineSegment(sketch, "E6.9.86.0", {"start": v(-12.9, 11.06) * mm, "end": v(-13.23, 11.85) * mm});
            skLineSegment(sketch, "E6.1.87.0", {"start": v(-11.39, 11.58) * mm, "end": v(-11.65, 12.38) * mm});
            skLineSegment(sketch, "E6.3.87.0", {"start": v(-12.18, 11.86) * mm, "end": v(-11.39, 11.58) * mm});
            skLineSegment(sketch, "E6.6.87.0", {"start": v(-12.45, 12.67) * mm, "end": v(-11.65, 12.38) * mm});
            skLineSegment(sketch, "E6.9.87.0", {"start": v(-12.18, 11.86) * mm, "end": v(-12.45, 12.67) * mm});
            skLineSegment(sketch, "E6.1.88.0", {"start": v(-10.63, 12.28) * mm, "end": v(-10.84, 13.1) * mm});
            skLineSegment(sketch, "E6.3.88.0", {"start": v(-11.4, 12.6) * mm, "end": v(-10.63, 12.28) * mm});
            skLineSegment(sketch, "E6.6.88.0", {"start": v(-11.63, 13.43) * mm, "end": v(-10.84, 13.1) * mm});
            skLineSegment(sketch, "E6.9.88.0", {"start": v(-11.4, 12.6) * mm, "end": v(-11.63, 13.43) * mm});
            skLineSegment(sketch, "E6.1.89.0", {"start": v(-9.84, 12.93) * mm, "end": v(-10, 13.75) * mm});
            skLineSegment(sketch, "E6.3.89.0", {"start": v(-10.59, 13.3) * mm, "end": v(-9.84, 12.93) * mm});
            skLineSegment(sketch, "E6.6.89.0", {"start": v(-10.75, 14.14) * mm, "end": v(-10, 13.75) * mm});
            skLineSegment(sketch, "E6.9.89.0", {"start": v(-10.59, 13.3) * mm, "end": v(-10.75, 14.14) * mm});
            skLineSegment(sketch, "E6.1.90.0", {"start": v(-9, 13.53) * mm, "end": v(-9.1, 14.36) * mm});
            skLineSegment(sketch, "E6.3.90.0", {"start": v(-9.73, 13.94) * mm, "end": v(-9, 13.53) * mm});
            skLineSegment(sketch, "E6.6.90.0", {"start": v(-9.84, 14.79) * mm, "end": v(-9.1, 14.36) * mm});
            skLineSegment(sketch, "E6.9.90.0", {"start": v(-9.73, 13.94) * mm, "end": v(-9.84, 14.79) * mm});
            skLineSegment(sketch, "E6.1.91.0", {"start": v(-8.13, 14.07) * mm, "end": v(-8.18, 14.9) * mm});
            skLineSegment(sketch, "E6.3.91.0", {"start": v(-8.83, 14.53) * mm, "end": v(-8.13, 14.07) * mm});
            skLineSegment(sketch, "E6.6.91.0", {"start": v(-8.88, 15.38) * mm, "end": v(-8.18, 14.9) * mm});
            skLineSegment(sketch, "E6.9.91.0", {"start": v(-8.83, 14.53) * mm, "end": v(-8.88, 15.38) * mm});
            skLineSegment(sketch, "E6.1.92.0", {"start": v(-7.22, 14.55) * mm, "end": v(-7.22, 15.4) * mm});
            skLineSegment(sketch, "E6.3.92.0", {"start": v(-7.89, 15.06) * mm, "end": v(-7.22, 14.55) * mm});
            skLineSegment(sketch, "E6.6.92.0", {"start": v(-7.9, 15.91) * mm, "end": v(-7.22, 15.4) * mm});
            skLineSegment(sketch, "E6.9.92.0", {"start": v(-7.89, 15.06) * mm, "end": v(-7.9, 15.91) * mm});
            skLineSegment(sketch, "E6.1.93.0", {"start": v(-6.28, 14.98) * mm, "end": v(-6.23, 15.82) * mm});
            skLineSegment(sketch, "E6.3.93.0", {"start": v(-6.92, 15.53) * mm, "end": v(-6.28, 14.98) * mm});
            skLineSegment(sketch, "E6.6.93.0", {"start": v(-6.87, 16.38) * mm, "end": v(-6.23, 15.82) * mm});
            skLineSegment(sketch, "E6.9.93.0", {"start": v(-6.92, 15.53) * mm, "end": v(-6.87, 16.38) * mm});
            skLineSegment(sketch, "E6.1.94.0", {"start": v(-5.32, 15.35) * mm, "end": v(-5.22, 16.18) * mm});
            skLineSegment(sketch, "E6.3.94.0", {"start": v(-5.92, 15.93) * mm, "end": v(-5.32, 15.35) * mm});
            skLineSegment(sketch, "E6.6.94.0", {"start": v(-5.82, 16.78) * mm, "end": v(-5.22, 16.18) * mm});
            skLineSegment(sketch, "E6.9.94.0", {"start": v(-5.92, 15.93) * mm, "end": v(-5.82, 16.78) * mm});
            skLineSegment(sketch, "E6.1.95.0", {"start": v(-4.34, 15.65) * mm, "end": v(-4.18, 16.48) * mm});
            skLineSegment(sketch, "E6.3.95.0", {"start": v(-4.9, 16.28) * mm, "end": v(-4.34, 15.65) * mm});
            skLineSegment(sketch, "E6.6.95.0", {"start": v(-4.75, 17.12) * mm, "end": v(-4.18, 16.48) * mm});
            skLineSegment(sketch, "E6.9.95.0", {"start": v(-4.9, 16.28) * mm, "end": v(-4.75, 17.12) * mm});
            skLineSegment(sketch, "E6.1.96.0", {"start": v(-3.34, 15.9) * mm, "end": v(-3.13, 16.7) * mm});
            skLineSegment(sketch, "E6.3.96.0", {"start": v(-3.87, 16.55) * mm, "end": v(-3.34, 15.9) * mm});
            skLineSegment(sketch, "E6.6.96.0", {"start": v(-3.66, 17.38) * mm, "end": v(-3.13, 16.7) * mm});
            skLineSegment(sketch, "E6.9.96.0", {"start": v(-3.87, 16.55) * mm, "end": v(-3.66, 17.38) * mm});
            skLineSegment(sketch, "E6.1.97.0", {"start": v(-2.33, 16.08) * mm, "end": v(-2.07, 16.87) * mm});
            skLineSegment(sketch, "E6.3.97.0", {"start": v(-2.81, 16.77) * mm, "end": v(-2.33, 16.08) * mm});
            skLineSegment(sketch, "E6.6.97.0", {"start": v(-2.55, 17.58) * mm, "end": v(-2.07, 16.87) * mm});
            skLineSegment(sketch, "E6.9.97.0", {"start": v(-2.81, 16.77) * mm, "end": v(-2.55, 17.58) * mm});
            skLineSegment(sketch, "E6.1.98.0", {"start": v(-1.31, 16.2) * mm, "end": v(-1, 16.97) * mm});
            skLineSegment(sketch, "E6.3.98.0", {"start": v(-1.74, 16.91) * mm, "end": v(-1.31, 16.2) * mm});
            skLineSegment(sketch, "E6.6.98.0", {"start": v(-1.43, 17.7) * mm, "end": v(-1, 16.97) * mm});
            skLineSegment(sketch, "E6.9.98.0", {"start": v(-1.74, 16.91) * mm, "end": v(-1.43, 17.7) * mm});
            skLineSegment(sketch, "E6.1.99.0", {"start": v(-0.28, 16.24) * mm, "end": v(0.08, 17) * mm});
            skLineSegment(sketch, "E6.3.99.0", {"start": v(-0.67, 16.99) * mm, "end": v(-0.28, 16.24) * mm});
            skLineSegment(sketch, "E6.6.99.0", {"start": v(-0.3, 17.76) * mm, "end": v(0.08, 17) * mm});
            skLineSegment(sketch, "E6.9.99.0", {"start": v(-0.67, 16.99) * mm, "end": v(-0.3, 17.76) * mm});
            skSolve(sketch);
        }
        {
            var Q0;
            Q0 = qSketchRegion(id + "F2", true);
            extrude(context, id + "F3", {"entities" : qUnion([Q0]), "operationType" : NewBodyOperationType.REMOVE, "endBound" : BoundingType.THROUGH_ALL, "oppositeDirection" : true, "depth" : 25 * mm, "offsetDistance" : 25 * mm});
        }
        {
            var Q0;
            Q0=makeQuery(id+"F1.opExtrude","CAP_FACE",FACE,{"disambiguationData":[OSD([sQuery(id+"F0.wireOp",EDGE,"E0")])],"isStart":true});
            var sketch = newSketch(context, id + "F4", { "sketchPlane" : qUnion([Q0])});
            skCircle(sketch, "E7", {"center": v(0, 0) * mm, "radius": 2.5 * mm});
            skSolve(sketch);
        }
        {
            var Q0;
            Q0 = qSketchRegion(id + "F4", true);
            extrude(context, id + "F5", {"entities" : qUnion([Q0]), "operationType" : NewBodyOperationType.ADD, "depth" : 3.5 * mm, "offsetDistance" : 25 * mm});
        }
        {
            var Q0;
            Q0=makeQuery(id+"F1.opExtrude","CAP_FACE",FACE,{"disambiguationData":[OSD([sQuery(id+"F0.wireOp",EDGE,"E0")])],"isStart":true});
            var sketch = newSketch(context, id + "F6", { "sketchPlane" : qUnion([Q0])});
            skCircle(sketch, "E8", {"center": v(0, 0) * mm, "radius": 4 * mm});
            skSolve(sketch);
        }
        {
            var Q0;
            Q0 = qSketchRegion(id + "F6", true);
            extrude(context, id + "F7", {"entities" : qUnion([Q0]), "operationType" : NewBodyOperationType.ADD, "depth" : 0.75 * mm, "offsetDistance" : 25 * mm});
        }
        {
            var Q0;
            Q0=makeQuery(id+"F1.opExtrude","CAP_FACE",FACE,{"disambiguationData":[OSD([sQuery(id+"F0.wireOp",EDGE,"E0")])],"isStart":false});
            var sketch = newSketch(context, id + "F8", { "sketchPlane" : qUnion([Q0])});
            skCircle(sketch, "E9", {"center": v(0, 0) * mm, "radius": 4 * mm});
            skSolve(sketch);
        }
        {
            var Q0;
            Q0 = qSketchRegion(id + "F8", true);
            extrude(context, id + "F9", {"entities" : qUnion([Q0]), "operationType" : NewBodyOperationType.ADD, "depth" : 10.5 * mm, "offsetDistance" : 25 * mm});
        }
        {
            var Q0;
            Q0=makeQuery(id+"F9.opExtrude","CAP_FACE",FACE,{"disambiguationData":[OSD([sQuery(id+"F8.wireOp",EDGE,"E9")])],"isStart":false});
            var sketch = newSketch(context, id + "F10", { "sketchPlane" : qUnion([Q0])});
            skCircle(sketch, "E10", {"center": v(0, 0) * mm, "radius": 2.5 * mm});
            skSolve(sketch);
        }
        {
            var Q0;
            Q0 = qSketchRegion(id + "F10", true);
            extrude(context, id + "F11", {"entities" : qUnion([Q0]), "operationType" : NewBodyOperationType.ADD, "depth" : 2.5 * mm, "offsetDistance" : 25 * mm});
        }
        {
            var Q0;
            Q0=makeQuery(id+"F11.opExtrude","CAP_FACE",FACE,{"disambiguationData":[OSD([sQuery(id+"F10.wireOp",EDGE,"E10")])],"isStart":false});
            var sketch = newSketch(context, id + "F12", { "sketchPlane" : qUnion([Q0])});
            skCircle(sketch, "E11", {"center": v(0, 0) * mm, "radius": 1.65 * mm});
            skSolve(sketch);
        }
        {
            var Q0;
            Q0 = qSketchRegion(id + "F12", true);
            extrude(context, id + "F13", {"entities" : qUnion([Q0]), "operationType" : NewBodyOperationType.REMOVE, "endBound" : BoundingType.THROUGH_ALL, "oppositeDirection" : true, "depth" : 25 * mm, "offsetDistance" : 25 * mm});
        }
    });
